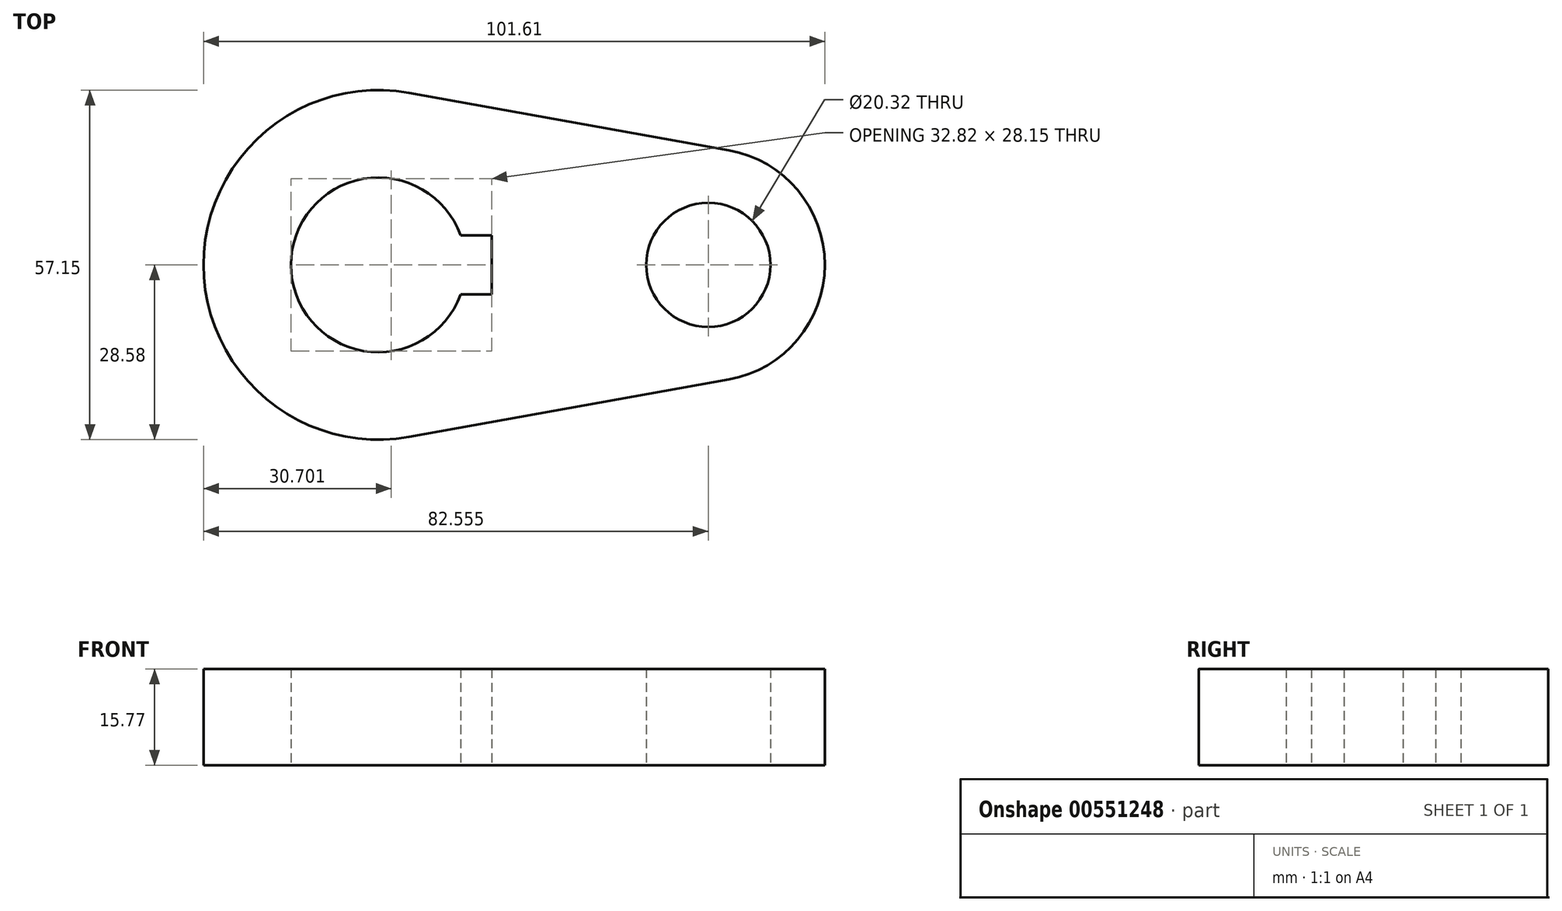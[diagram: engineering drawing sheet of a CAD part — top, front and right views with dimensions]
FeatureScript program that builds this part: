
annotation { "Feature Type Name" : "Feature", "Feature Type Description" : "" }
export const myFeature = defineFeature(function(context is Context, id is Id, definition is map)
    precondition{}
    {
        {
            var Q0;
            Q0=qCreatedBy(makeId("Top.planeOp"),FACE);
            var sketch = newSketch(context, id + "F0", { "sketchPlane" : qUnion([Q0])});
            skArc(sketch, "E0", {"start": v(13.45, 4.83) * mm, "mid": v(-14.29, 0) * mm, "end": v(13.45, -4.83) * mm});
            skArc(sketch, "E1", {"start": v(57.34, -18.75) * mm, "mid": v(73.03, 0) * mm, "end": v(57.34, 18.75) * mm});
            skCircle(sketch, "E2", {"center": v(0, 0) * mm, "radius": 28.58 * mm});
            skLineSegment(sketch, "E3", {"start": v(5.04, 28.13) * mm, "end": v(57.34, 18.75) * mm});
            skLineSegment(sketch, "E4", {"start": v(5.04, -28.13) * mm, "end": v(57.34, -18.75) * mm});
            skCircle(sketch, "E5", {"center": v(53.98, 0) * mm, "radius": 10.16 * mm});
            skLineSegment(sketch, "E6", {"start": v(13.45, 4.83) * mm, "end": v(18.53, 4.83) * mm});
            skLineSegment(sketch, "E7", {"start": v(18.53, 4.83) * mm, "end": v(18.53, -4.83) * mm});
            skLineSegment(sketch, "E8", {"start": v(18.53, -4.83) * mm, "end": v(13.45, -4.83) * mm});
            skSolve(sketch);
        }
        {
            var Q0;
            Q0=makeQuery(id+"F0.imprint","IMPRINT",FACE,{"disambiguationData":[TD([[makeQuery(id+"F0.imprint","IMPRINT",EDGE,{"derivedFrom":sQuery(id+"F0.wireOp",EDGE,"E0")}),-1.0]])]});
            var Q1;
            Q1=makeQuery(id+"F0.imprint","IMPRINT",FACE,{"disambiguationData":[TD([[makeQuery(id+"F0.imprint","IMPRINT",EDGE,{"derivedFrom":sQuery(id+"F0.wireOp",EDGE,"E1")}),1.0]])]});
            extrude(context, id + "F1", {"entities" : qUnion([Q0, Q1]), "depth" : 15.77 * mm, "offsetDistance" : 25.4 * mm});
        }
    });
